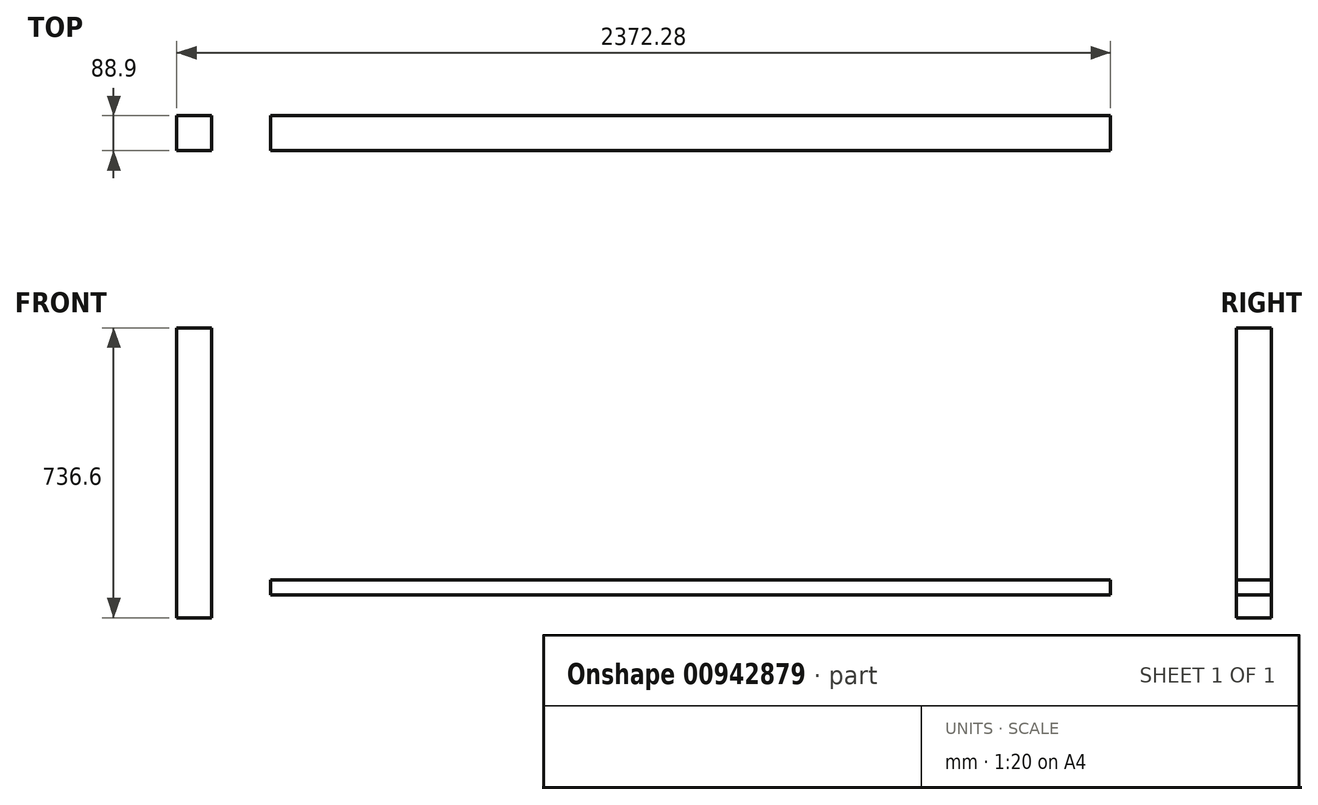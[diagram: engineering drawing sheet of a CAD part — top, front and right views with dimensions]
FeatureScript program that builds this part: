
annotation { "Feature Type Name" : "Feature", "Feature Type Description" : "" }
export const myFeature = defineFeature(function(context is Context, id is Id, definition is map)
    precondition{}
    {
        {
            var Q0;
            Q0=qCreatedBy(makeId("Front.planeOp"),FACE);
            var sketch = newSketch(context, id + "F0", { "sketchPlane" : qUnion([Q0])});
            skLineSegment(sketch, "E0.bottom", {"start": v(0, 0) * mm, "end": v(88.9, 0) * mm});
            skLineSegment(sketch, "E0.top", {"start": v(0, -736.6) * mm, "end": v(88.9, -736.6) * mm});
            skLineSegment(sketch, "E0.left", {"start": v(0, 0) * mm, "end": v(0, -736.6) * mm});
            skLineSegment(sketch, "E0.right", {"start": v(88.9, 0) * mm, "end": v(88.9, -736.6) * mm});
            skSolve(sketch);
        }
        {
            var Q0;
            Q0 = qSketchRegion(id + "F0", true);
            extrude(context, id + "F1", {"entities" : qUnion([Q0]), "depth" : 88.9 * mm, "offsetDistance" : 25.4 * mm});
        }
        {
            var Q0;
            Q0=qCreatedBy(makeId("Front.planeOp"),FACE);
            var sketch = newSketch(context, id + "F2", { "sketchPlane" : qUnion([Q0])});
            skLineSegment(sketch, "E1", {"start": v(238.68, -640.51) * mm, "end": v(2372.28, -640.51) * mm});
            skLineSegment(sketch, "E2", {"start": v(2372.28, -640.51) * mm, "end": v(2372.28, -678.61) * mm});
            skLineSegment(sketch, "E3", {"start": v(2372.28, -678.61) * mm, "end": v(238.68, -678.61) * mm});
            skLineSegment(sketch, "E4", {"start": v(238.68, -678.61) * mm, "end": v(238.68, -640.51) * mm});
            skSolve(sketch);
        }
        {
            var Q0;
            Q0 = qSketchRegion(id + "F2", true);
            extrude(context, id + "F3", {"entities" : qUnion([Q0]), "depth" : 88.9 * mm, "offsetDistance" : 25.4 * mm});
        }
    });
